FCSTD DOCUMENT  (FreeCAD 1.0R39319 (Git))
Label: 2BHK_Apartment_with_Parking
License: All rights reserved
LicenseURL: https://en.wikipedia.org/wiki/All_rights_reserved
objects: Part::Part2DObjectPython×30, App::FeaturePython×25
note: 30 computed .brp shape members not serialized (recipe doc carries the construction recipe); baked Part::Feature solids carry a one-line shape summary decoded from their .brp

FEATURE [Part::Part2DObjectPython] Wire  # Draft 2D object (typed FeaturePython)
  Area = 180000000
  ChamferSize = 0
  Closed = true
  End = (0,0,0)
  FilletRadius = 0
  Length = 54000
  MakeFace = true
  Points = (5) [(0,0,0),(15000,0,0),(15000,12000,0),(0,12000,0),(0,0,0)]
  Start = (0,0,0)
  Subdivisions = 0
FEATURE [Part::Part2DObjectPython] Rectangle  # Draft 2D object (typed FeaturePython)
  Area = 20000000
  ChamferSize = 0
  Columns = 1
  FilletRadius = 0
  Height = 4000
  Length = 5000
  MakeFace = true
  Placement = pos=(1000,6000,0) rot=(0,0,1;0rad)
  Rows = 1
FEATURE [App::FeaturePython] Text  # WARN: FeaturePython — macro-defined, semantics opaque (R4)
  Placement = pos=(2666,8000,0) rot=(0,0,1;0rad)
  Text = Living Room | 20 sqm
FEATURE [Part::Part2DObjectPython] Rectangle001  # Draft 2D object (typed FeaturePython)
  Area = 1.4e+07
  ChamferSize = 0
  Columns = 1
  FilletRadius = 0
  Height = 3500
  Length = 4000
  MakeFace = true
  Placement = pos=(1000,10500,0) rot=(0,0,1;0rad)
  Rows = 1
FEATURE [App::FeaturePython] Text001  # WARN: FeaturePython — macro-defined, semantics opaque (R4)
  Placement = pos=(2333,12250,0) rot=(0,0,1;0rad)
  Text = Master Bedroom | 14 sqm
FEATURE [Part::Part2DObjectPython] Rectangle002  # Draft 2D object (typed FeaturePython)
  Area = 1.05e+07
  ChamferSize = 0
  Columns = 1
  FilletRadius = 0
  Height = 3000
  Length = 3500
  MakeFace = true
  Placement = pos=(6000,10500,0) rot=(0,0,1;0rad)
  Rows = 1
FEATURE [App::FeaturePython] Text002  # WARN: FeaturePython — macro-defined, semantics opaque (R4)
  Placement = pos=(7166,12000,0) rot=(0,0,1;0rad)
  Text = Bedroom 2 | 10.5 sqm
FEATURE [Part::Part2DObjectPython] Rectangle003  # Draft 2D object (typed FeaturePython)
  Area = 8.75e+06
  ChamferSize = 0
  Columns = 1
  FilletRadius = 0
  Height = 2500
  Length = 3500
  MakeFace = true
  Placement = pos=(7000,6000,0) rot=(0,0,1;0rad)
  Rows = 1
FEATURE [App::FeaturePython] Text003  # WARN: FeaturePython — macro-defined, semantics opaque (R4)
  Placement = pos=(8166,7250,0) rot=(0,0,1;0rad)
  Text = Kitchen | 8.75 sqm
FEATURE [Part::Part2DObjectPython] Rectangle004  # Draft 2D object (typed FeaturePython)
  Area = 5000000
  ChamferSize = 0
  Columns = 1
  FilletRadius = 0
  Height = 2000
  Length = 2500
  MakeFace = true
  Placement = pos=(11000,6000,0) rot=(0,0,1;0rad)
  Rows = 1
FEATURE [App::FeaturePython] Text004  # WARN: FeaturePython — macro-defined, semantics opaque (R4)
  Placement = pos=(11833,7000,0) rot=(0,0,1;0rad)
  Text = Bathroom 1 | 5 sqm
FEATURE [Part::Part2DObjectPython] Rectangle005  # Draft 2D object (typed FeaturePython)
  Area = 3.6e+06
  ChamferSize = 0
  Columns = 1
  FilletRadius = 0
  Height = 1800
  Length = 2000
  MakeFace = true
  Placement = pos=(5200,10500,0) rot=(0,0,1;0rad)
  Rows = 1
FEATURE [App::FeaturePython] Text005  # WARN: FeaturePython — macro-defined, semantics opaque (R4)
  Placement = pos=(5866,11400,0) rot=(0,0,1;0rad)
  Text = Bathroom 2 | 3.6 sqm
FEATURE [Part::Part2DObjectPython] Rectangle006  # Draft 2D object (typed FeaturePython)
  Area = 12500000
  ChamferSize = 0
  Columns = 1
  FilletRadius = 0
  Height = 2500
  Length = 5000
  MakeFace = true
  Placement = pos=(1000,1000,0) rot=(0,0,1;0rad)
  Rows = 1
FEATURE [App::FeaturePython] Text006  # WARN: FeaturePython — macro-defined, semantics opaque (R4)
  Placement = pos=(2666,2250,0) rot=(0,0,1;0rad)
  Text = Parking | 12.5 sqm
FEATURE [Part::Part2DObjectPython] Line  # Draft 2D object (typed FeaturePython)
  Area = 0
  ChamferSize = 0
  Closed = false
  End = (8400,0,0)
  FilletRadius = 0
  Length = 900
  MakeFace = true
  Points = (2) [(7500,0,0),(8400,0,0)]
  Start = (7500,0,0)
  Subdivisions = 0
FEATURE [Part::Part2DObjectPython] Line001  # Draft 2D object (typed FeaturePython)
  Area = 0
  ChamferSize = 0
  Closed = false
  End = (5600,6000,0)
  FilletRadius = 0
  Length = 800
  MakeFace = true
  Points = (2) [(4800,6000,0),(5600,6000,0)]
  Start = (4800,6000,0)
  Subdivisions = 0
FEATURE [Part::Part2DObjectPython] Line002  # Draft 2D object (typed FeaturePython)
  Area = 0
  ChamferSize = 0
  Closed = false
  End = (6800,10700,0)
  FilletRadius = 0
  Length = 800
  MakeFace = true
  Points = (2) [(6000,10700,0),(6800,10700,0)]
  Start = (6000,10700,0)
  Subdivisions = 0
FEATURE [Part::Part2DObjectPython] Rectangle007  # Draft 2D object (typed FeaturePython)
  Area = 144000
  ChamferSize = 0
  Columns = 1
  FilletRadius = 0
  Height = 120
  Length = 1200
  MakeFace = true
  Placement = pos=(3000,12000,0) rot=(0,0,1;0rad)
  Rows = 1
FEATURE [Part::Part2DObjectPython] Rectangle008  # Draft 2D object (typed FeaturePython)
  Area = 144000
  ChamferSize = 0
  Columns = 1
  FilletRadius = 0
  Height = 120
  Length = 1200
  MakeFace = true
  Placement = pos=(8000,12000,0) rot=(0,0,1;0rad)
  Rows = 1
FEATURE [Part::Part2DObjectPython] Rectangle009  # Draft 2D object (typed FeaturePython)
  Area = 120000
  ChamferSize = 0
  Columns = 1
  FilletRadius = 0
  Height = 120
  Length = 1000
  MakeFace = true
  Placement = pos=(0,7000,0) rot=(0,0,1;0rad)
  Rows = 1
FEATURE [App::FeaturePython] Dimension  # Draft dimension (typed FeaturePython)
  Diameter = false
  Dimline = (7500,-800,0)
  Direction = (0,0,0)
  Distance = 15000
  End = (15000,-800,0)
  Normal = (0,0,1)
  Start = (0,-800,0)
FEATURE [App::FeaturePython] Dimension001  # Draft dimension (typed FeaturePython)
  Diameter = false
  Dimline = (-800,6000,0)
  Direction = (0,0,0)
  Distance = 12000
  End = (-800,12000,0)
  Normal = (0,0,1)
  Start = (-800,0,0)
FEATURE [Part::Part2DObjectPython] Line003  # Draft 2D object (typed FeaturePython)
  Area = 0
  ChamferSize = 0
  Closed = false
  End = (0,13500,0)
  FilletRadius = 0
  Length = 15000
  MakeFace = true
  Points = (2) [(0,-1500,0),(0,13500,0)]
  Start = (0,-1500,0)
  Subdivisions = 0
FEATURE [App::FeaturePython] Text007  # WARN: FeaturePython — macro-defined, semantics opaque (R4)
  Placement = pos=(-100,-2000,0) rot=(0,0,1;0rad)
  Text = A
FEATURE [Part::Part2DObjectPython] Line004  # Draft 2D object (typed FeaturePython)
  Area = 0
  ChamferSize = 0
  Closed = false
  End = (2000,13500,0)
  FilletRadius = 0
  Length = 15000
  MakeFace = true
  Points = (2) [(2000,-1500,0),(2000,13500,0)]
  Start = (2000,-1500,0)
  Subdivisions = 0
FEATURE [App::FeaturePython] Text008  # WARN: FeaturePython — macro-defined, semantics opaque (R4)
  Placement = pos=(1900,-2000,0) rot=(0,0,1;0rad)
  Text = B
FEATURE [Part::Part2DObjectPython] Line005  # Draft 2D object (typed FeaturePython)
  Area = 0
  ChamferSize = 0
  Closed = false
  End = (4000,13500,0)
  FilletRadius = 0
  Length = 15000
  MakeFace = true
  Points = (2) [(4000,-1500,0),(4000,13500,0)]
  Start = (4000,-1500,0)
  Subdivisions = 0
FEATURE [App::FeaturePython] Text009  # WARN: FeaturePython — macro-defined, semantics opaque (R4)
  Placement = pos=(3900,-2000,0) rot=(0,0,1;0rad)
  Text = C
FEATURE [Part::Part2DObjectPython] Line006  # Draft 2D object (typed FeaturePython)
  Area = 0
  ChamferSize = 0
  Closed = false
  End = (6000,13500,0)
  FilletRadius = 0
  Length = 15000
  MakeFace = true
  Points = (2) [(6000,-1500,0),(6000,13500,0)]
  Start = (6000,-1500,0)
  Subdivisions = 0
FEATURE [App::FeaturePython] Text010  # WARN: FeaturePython — macro-defined, semantics opaque (R4)
  Placement = pos=(5900,-2000,0) rot=(0,0,1;0rad)
  Text = D
FEATURE [Part::Part2DObjectPython] Line007  # Draft 2D object (typed FeaturePython)
  Area = 0
  ChamferSize = 0
  Closed = false
  End = (8000,13500,0)
  FilletRadius = 0
  Length = 15000
  MakeFace = true
  Points = (2) [(8000,-1500,0),(8000,13500,0)]
  Start = (8000,-1500,0)
  Subdivisions = 0
FEATURE [App::FeaturePython] Text011  # WARN: FeaturePython — macro-defined, semantics opaque (R4)
  Placement = pos=(7900,-2000,0) rot=(0,0,1;0rad)
  Text = E
FEATURE [Part::Part2DObjectPython] Line008  # Draft 2D object (typed FeaturePython)
  Area = 0
  ChamferSize = 0
  Closed = false
  End = (10000,13500,0)
  FilletRadius = 0
  Length = 15000
  MakeFace = true
  Points = (2) [(10000,-1500,0),(10000,13500,0)]
  Start = (10000,-1500,0)
  Subdivisions = 0
FEATURE [App::FeaturePython] Text012  # WARN: FeaturePython — macro-defined, semantics opaque (R4)
  Placement = pos=(9900,-2000,0) rot=(0,0,1;0rad)
  Text = F
FEATURE [Part::Part2DObjectPython] Line009  # Draft 2D object (typed FeaturePython)
  Area = 0
  ChamferSize = 0
  Closed = false
  End = (12000,13500,0)
  FilletRadius = 0
  Length = 15000
  MakeFace = true
  Points = (2) [(12000,-1500,0),(12000,13500,0)]
  Start = (12000,-1500,0)
  Subdivisions = 0
FEATURE [App::FeaturePython] Text013  # WARN: FeaturePython — macro-defined, semantics opaque (R4)
  Placement = pos=(11900,-2000,0) rot=(0,0,1;0rad)
  Text = G
FEATURE [Part::Part2DObjectPython] Line010  # Draft 2D object (typed FeaturePython)
  Area = 0
  ChamferSize = 0
  Closed = false
  End = (14000,13500,0)
  FilletRadius = 0
  Length = 15000
  MakeFace = true
  Points = (2) [(14000,-1500,0),(14000,13500,0)]
  Start = (14000,-1500,0)
  Subdivisions = 0
FEATURE [App::FeaturePython] Text014  # WARN: FeaturePython — macro-defined, semantics opaque (R4)
  Placement = pos=(13900,-2000,0) rot=(0,0,1;0rad)
  Text = H
FEATURE [Part::Part2DObjectPython] Line011  # Draft 2D object (typed FeaturePython)
  Area = 0
  ChamferSize = 0
  Closed = false
  End = (16000,13500,0)
  FilletRadius = 0
  Length = 15000
  MakeFace = true
  Points = (2) [(16000,-1500,0),(16000,13500,0)]
  Start = (16000,-1500,0)
  Subdivisions = 0
FEATURE [Part::Part2DObjectPython] Line012  # Draft 2D object (typed FeaturePython)
  Area = 0
  ChamferSize = 0
  Closed = false
  End = (16500,0,0)
  FilletRadius = 0
  Length = 18000
  MakeFace = true
  Points = (2) [(-1500,0,0),(16500,0,0)]
  Start = (-1500,0,0)
  Subdivisions = 0
FEATURE [App::FeaturePython] Text015  # WARN: FeaturePython — macro-defined, semantics opaque (R4)
  Placement = pos=(-2200,-100,0) rot=(0,0,1;0rad)
  Text = 1
FEATURE [Part::Part2DObjectPython] Line013  # Draft 2D object (typed FeaturePython)
  Area = 0
  ChamferSize = 0
  Closed = false
  End = (16500,2000,0)
  FilletRadius = 0
  Length = 18000
  MakeFace = true
  Points = (2) [(-1500,2000,0),(16500,2000,0)]
  Start = (-1500,2000,0)
  Subdivisions = 0
FEATURE [App::FeaturePython] Text016  # WARN: FeaturePython — macro-defined, semantics opaque (R4)
  Placement = pos=(-2200,1900,0) rot=(0,0,1;0rad)
  Text = 2
FEATURE [Part::Part2DObjectPython] Line014  # Draft 2D object (typed FeaturePython)
  Area = 0
  ChamferSize = 0
  Closed = false
  End = (16500,4000,0)
  FilletRadius = 0
  Length = 18000
  MakeFace = true
  Points = (2) [(-1500,4000,0),(16500,4000,0)]
  Start = (-1500,4000,0)
  Subdivisions = 0
FEATURE [App::FeaturePython] Text017  # WARN: FeaturePython — macro-defined, semantics opaque (R4)
  Placement = pos=(-2200,3900,0) rot=(0,0,1;0rad)
  Text = 3
FEATURE [Part::Part2DObjectPython] Line015  # Draft 2D object (typed FeaturePython)
  Area = 0
  ChamferSize = 0
  Closed = false
  End = (16500,6000,0)
  FilletRadius = 0
  Length = 18000
  MakeFace = true
  Points = (2) [(-1500,6000,0),(16500,6000,0)]
  Start = (-1500,6000,0)
  Subdivisions = 0
FEATURE [App::FeaturePython] Text018  # WARN: FeaturePython — macro-defined, semantics opaque (R4)
  Placement = pos=(-2200,5900,0) rot=(0,0,1;0rad)
  Text = 4
FEATURE [Part::Part2DObjectPython] Line016  # Draft 2D object (typed FeaturePython)
  Area = 0
  ChamferSize = 0
  Closed = false
  End = (16500,8000,0)
  FilletRadius = 0
  Length = 18000
  MakeFace = true
  Points = (2) [(-1500,8000,0),(16500,8000,0)]
  Start = (-1500,8000,0)
  Subdivisions = 0
FEATURE [App::FeaturePython] Text019  # WARN: FeaturePython — macro-defined, semantics opaque (R4)
  Placement = pos=(-2200,7900,0) rot=(0,0,1;0rad)
  Text = 5
FEATURE [Part::Part2DObjectPython] Line017  # Draft 2D object (typed FeaturePython)
  Area = 0
  ChamferSize = 0
  Closed = false
  End = (16500,10000,0)
  FilletRadius = 0
  Length = 18000
  MakeFace = true
  Points = (2) [(-1500,10000,0),(16500,10000,0)]
  Start = (-1500,10000,0)
  Subdivisions = 0
FEATURE [App::FeaturePython] Text020  # WARN: FeaturePython — macro-defined, semantics opaque (R4)
  Placement = pos=(-2200,9900,0) rot=(0,0,1;0rad)
  Text = 6
FEATURE [Part::Part2DObjectPython] Line018  # Draft 2D object (typed FeaturePython)
  Area = 0
  ChamferSize = 0
  Closed = false
  End = (16500,12000,0)
  FilletRadius = 0
  Length = 18000
  MakeFace = true
  Points = (2) [(-1500,12000,0),(16500,12000,0)]
  Start = (-1500,12000,0)
  Subdivisions = 0
FEATURE [App::FeaturePython] Text021  # WARN: FeaturePython — macro-defined, semantics opaque (R4)
  Placement = pos=(-2200,11900,0) rot=(0,0,1;0rad)
  Text = 7
FEATURE [App::FeaturePython] Text022  # WARN: FeaturePython — macro-defined, semantics opaque (R4)
  Placement = pos=(9000,-2500,0) rot=(0,0,1;0rad)
  Text = 2BHK Apartment with Parking | Scale: 1:100 | Total Area: 95 sqm
